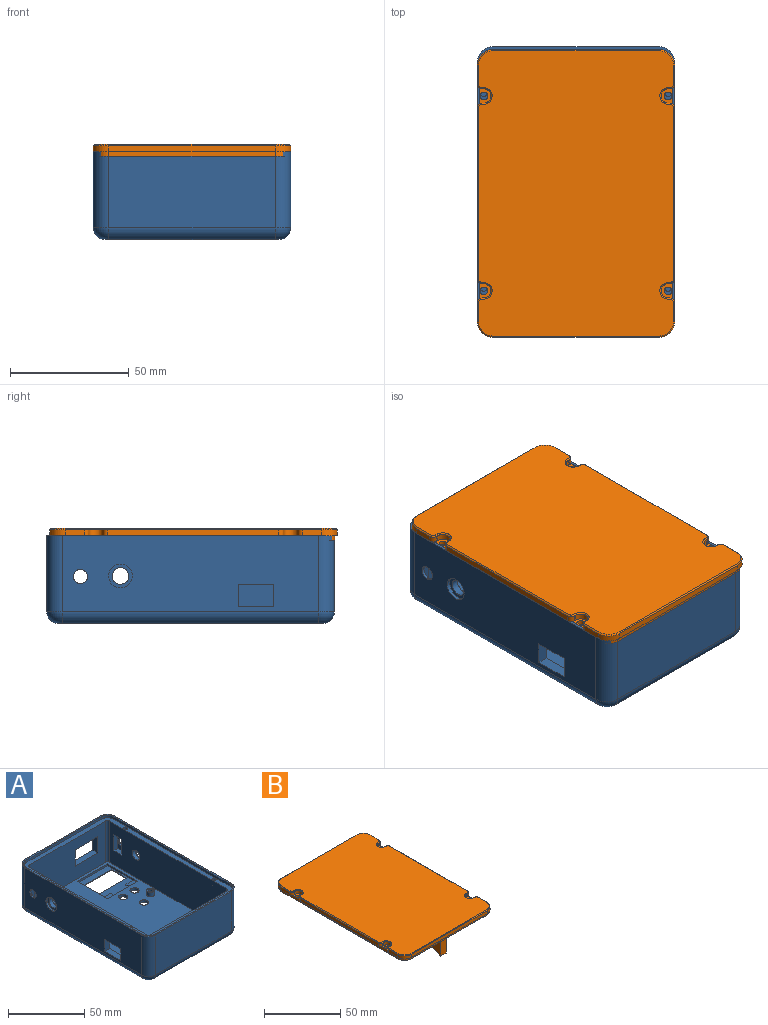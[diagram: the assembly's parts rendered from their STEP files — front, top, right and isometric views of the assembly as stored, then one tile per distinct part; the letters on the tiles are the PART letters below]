
ASSEMBLY  parts=2 mates=1
PART A: 103 faces, bbox 83x121x37 mm
  f0: plane 119x81mm, normal (0,0,1), area 1303.8mm2, adj f4,f12,f13,f14,f15,f16,f17,f18
  f1: cylinder r=3.5mm len=7mm, axis (1,0,0), area 66mm2, adj f12,f61
  f2: cylinder r=3mm len=6mm, axis (-1,0,0), area 18.8mm2, adj f23,f59
  f3: cylinder r=3.5mm len=7mm, axis (-1,0,0), area 66mm2, adj f4,f54
  f4: plane 108x33mm, normal (1,0,0), area 3292.4mm2, adj f0,f3,f6,f17,f18,f48,f49,f50
  f5: cylinder r=3mm len=6mm, axis (1,0,0), area 18.8mm2, adj f19,f52
  f6: plane 112x74mm, normal (0,0,1), area 7272mm2, adj f4,f12,f13,f14,f15,f16,f17,f18
  f7: plane 26x0.5mm, normal (0,1,0), area 13mm2, adj f8,f9,f11,f38
  f8: plane 14x0.5mm, normal (1,0,0), area 7mm2, adj f7,f10,f11,f38
  f9: plane 14x0.5mm, normal (-1,0,0), area 7mm2, adj f7,f10,f11,f38
  f10: plane 26x0.5mm, normal (0,-1,0), area 13mm2, adj f8,f9,f11,f38
  f11: plane 111x73mm, normal (0,0,-1), area 7567.4mm2, adj f7,f8,f9,f10,f42,f43,f44,f45
  f12: plane 108x33mm, normal (-1,0,0), area 3434.9mm2, adj f0,f1,f6,f15,f16,f55,f56,f57
  f13: plane 70x33mm, normal (0,-1,0), area 2037mm2, adj f0,f6,f15,f18,f27,f28,f29,f30
  f14: plane 70x33mm, normal (0,1,0), area 2310mm2, adj f0,f6,f16,f17
  f15: cylinder r=2mm len=33mm, axis (0,0,-1), area 103.7mm2, adj f0,f6,f12,f13
  f16: cylinder r=2mm len=33mm, axis (0,0,-1), area 103.7mm2, adj f0,f6,f12,f14
  f17: cylinder r=2mm len=33mm, axis (0,0,-1), area 103.7mm2, adj f0,f4,f6,f14
  f18: cylinder r=2mm len=33mm, axis (0,0,-1), area 103.7mm2, adj f0,f4,f6,f13
  f19: plane 108x32mm, normal (-1,0,0), area 3206.7mm2, adj f5,f20,f26,f53,f70,f71,f72,f73
  f20: cylinder r=6.5mm len=32mm, axis (0,0,-1), area 326.7mm2, adj f19,f21,f70,f89
  f21: plane 70x32mm, normal (0,-1,0), area 2240mm2, adj f20,f22,f70,f87
  f22: cylinder r=6.5mm len=32mm, axis (0,0,-1), area 326.7mm2, adj f21,f23,f70,f85
  f23: plane 108x32mm, normal (1,0,0), area 3349.2mm2, adj f2,f22,f24,f60,f70,f84
  f24: cylinder r=6.5mm len=32mm, axis (0,0,-1), area 326.7mm2, adj f23,f25,f70,f86
  f25: plane 70x32mm, normal (0,1,0), area 1967mm2, adj f24,f26,f27,f28,f29,f30,f70,f88
  f26: cylinder r=6.5mm len=32mm, axis (0,0,-1), area 326.7mm2, adj f19,f25,f70,f90
  f27: plane 21x4.5mm, normal (0,0,1), area 94.5mm2, adj f13,f25,f28,f29
  f28: plane 13x4.5mm, normal (-1,0,0), area 58.5mm2, adj f13,f25,f27,f30
  f29: plane 13x4.5mm, normal (1,0,0), area 58.5mm2, adj f13,f25,f27,f30
  f30: plane 21x4.5mm, normal (0,0,-1), area 94.5mm2, adj f13,f25,f28,f29
  f31: plane 28x1.5mm, normal (-1,0,0), area 40mm2, adj f6,f35,f37,f38,f39,f41
  f32: plane 28x1.5mm, normal (1,0,0), area 40mm2, adj f6,f33,f35,f38,f40,f41
  f33: plane 7x0.5mm, normal (0,1,0), area 3.5mm2, adj f32,f34,f38,f40
  f34: plane 4x0.5mm, normal (1,0,0), area 2mm2, adj f33,f35,f38,f40
  f35: plane 28x1.5mm, normal (0,1,0), area 35mm2, adj f6,f31,f32,f34,f36,f38,f39,f40
  f36: plane 4x0.5mm, normal (-1,0,0), area 2mm2, adj f35,f37,f38,f39
  f37: plane 7x0.5mm, normal (0,1,0), area 3.5mm2, adj f31,f36,f38,f39
  f38: plane 28x28mm, normal (0,0,1), area 364mm2, adj f7,f8,f9,f10,f31,f32,f33,f34
  f39: plane 7x4mm, normal (0,0,1), area 28mm2, adj f31,f35,f36,f37
  f40: plane 7x4mm, normal (0,0,1), area 28mm2, adj f32,f33,f34,f35
  f41: plane 28x1.5mm, normal (0,-1,0), area 42mm2, adj f6,f31,f32,f38
  f42: cylinder r=3mm len=6mm, axis (0,0,1), area 37.7mm2, adj f6,f11
  f43: cylinder r=3mm len=6mm, axis (0,0,1), area 37.7mm2, adj f6,f11
  f44: cylinder r=3mm len=6mm, axis (0,0,1), area 37.7mm2, adj f6,f11
  f45: cylinder r=3mm len=6mm, axis (0,0,1), area 37.7mm2, adj f6,f11
  f46: cylinder r=3mm len=6mm, axis (0,0,1), area 37.7mm2, adj f6,f11
  f47: cylinder r=3mm len=6mm, axis (0,0,1), area 37.7mm2, adj f6,f11
  f48: plane 12.5x3.5mm, normal (0,-1,0), area 43.8mm2, adj f4,f49,f51,f52
  f49: plane 7.25x3.5mm, normal (0,0,-1), area 25.4mm2, adj f4,f48,f50,f52
  f50: plane 12.5x3.5mm, normal (0,1,0), area 43.8mm2, adj f4,f49,f51,f52
  f51: plane 7.25x3.5mm, normal (0,0,1), area 25.4mm2, adj f4,f48,f50,f52
  f52: plane 12.5x7.25mm, normal (1,0,0), area 62.4mm2, adj f5,f48,f49,f50,f51
  f53: cylinder r=5mm len=10mm, axis (-1,0,0), area 47.1mm2, adj f19,f54
  f54: plane 10x10mm, normal (-1,0,0), area 40.1mm2, adj f3,f53
  f55: plane 12.5x3.5mm, normal (0,-1,0), area 43.8mm2, adj f12,f56,f58,f59
  f56: plane 7.25x3.5mm, normal (0,0,1), area 25.4mm2, adj f12,f55,f57,f59
  f57: plane 12.5x3.5mm, normal (0,1,0), area 43.8mm2, adj f12,f56,f58,f59
  f58: plane 7.25x3.5mm, normal (0,0,-1), area 25.4mm2, adj f12,f55,f57,f59
  f59: plane 12.5x7.25mm, normal (-1,0,0), area 62.4mm2, adj f2,f55,f56,f57,f58
  f60: cylinder r=5mm len=10mm, axis (1,0,0), area 47.1mm2, adj f23,f61
  f61: plane 10x10mm, normal (1,0,0), area 40.1mm2, adj f1,f60
  f62: cylinder r=5.5mm len=5.5mm, axis (0,0,-1), area 17.3mm2, adj f0,f63,f69,f70
  f63: plane 108x2mm, normal (1,0,0), area 216mm2, adj f0,f62,f64,f70
  f64: cylinder r=5.5mm len=5.5mm, axis (0,0,-1), area 17.3mm2, adj f0,f63,f65,f70
  f65: plane 70x2mm, normal (0,-1,0), area 140mm2, adj f0,f64,f66,f70
  f66: cylinder r=5.5mm len=5.5mm, axis (0,0,-1), area 17.3mm2, adj f0,f65,f67,f70
  f67: plane 108x2mm, normal (-1,0,0), area 216mm2, adj f0,f66,f68,f70
  f68: cylinder r=5.5mm len=5.5mm, axis (0,0,-1), area 17.3mm2, adj f0,f67,f69,f70
  f69: plane 70x2mm, normal (0,1,0), area 140mm2, adj f0,f62,f68,f70
  f70: plane 121x83mm, normal (0,0,1), area 393.7mm2, adj f19,f20,f21,f22,f23,f24,f25,f26
  f71: plane 9.5x4.5mm, normal (0,1,0), area 42.8mm2, adj f4,f19,f72,f73
  f72: plane 15x4.5mm, normal (0,0,1), area 67.5mm2, adj f4,f19,f71,f74
  f73: plane 15x4.5mm, normal (0,0,-1), area 67.5mm2, adj f4,f19,f71,f74
  f74: plane 9.5x4.5mm, normal (0,-1,0), area 42.8mm2, adj f4,f19,f72,f73
  f75: cylinder r=1.45mm len=4.5mm, axis (0,0,-1), area 41mm2, adj f77,f102
  f76: cylinder r=2.5mm len=5mm, axis (0,0,-1), area 55mm2, adj f6,f77
  f77: plane 5x5mm, normal (0,0,1), area 13mm2, adj f75,f76
  f78: cylinder r=1.45mm len=4.5mm, axis (0,0,-1), area 41mm2, adj f80,f101
  f79: cylinder r=2.5mm len=5mm, axis (0,0,-1), area 55mm2, adj f6,f80
  f80: plane 5x5mm, normal (0,0,1), area 13mm2, adj f78,f79
  f81: cylinder r=1.45mm len=4.5mm, axis (0,0,-1), area 41mm2, adj f83,f100
  f82: cylinder r=2.5mm len=5mm, axis (0,0,-1), area 55mm2, adj f6,f83
  f83: plane 5x5mm, normal (0,0,1), area 13mm2, adj f81,f82
  f84: cylinder r=5mm len=108mm, axis (0,1,0), area 848.2mm2, adj f11,f23,f85,f86
  f85: torus R=1.5mm, axis (0,0,1), area 57.8mm2, adj f11,f22,f84,f87
  f86: torus R=1.5mm, axis (0,0,1), area 57.8mm2, adj f11,f24,f84,f88
  f87: cylinder r=5mm len=70mm, axis (1,0,0), area 549.8mm2, adj f11,f21,f85,f89
  f88: cylinder r=5mm len=70mm, axis (-1,0,0), area 549.8mm2, adj f11,f25,f86,f90
  f89: torus R=1.5mm, axis (0,0,1), area 57.8mm2, adj f11,f20,f87,f91
  f90: torus R=1.5mm, axis (0,0,1), area 57.8mm2, adj f11,f26,f88,f91
  f91: cylinder r=5mm len=108mm, axis (0,-1,0), area 848.2mm2, adj f11,f19,f89,f90
  f92: cylinder r=1.4mm len=4mm, axis (0,0,1), area 35.2mm2, adj f0,f93
  f93: plane 2.8x2.8mm, normal (0,0,1), area 6.2mm2, adj f92
  f94: cylinder r=1.4mm len=4mm, axis (0,0,1), area 35.2mm2, adj f0,f95
  f95: plane 2.8x2.8mm, normal (0,0,1), area 6.2mm2, adj f94
  f96: cylinder r=1.4mm len=4mm, axis (0,0,1), area 35.2mm2, adj f0,f97
  f97: plane 2.8x2.8mm, normal (0,0,1), area 6.2mm2, adj f96
  f98: cylinder r=1.4mm len=4mm, axis (0,0,1), area 35.2mm2, adj f0,f99
  f99: plane 2.8x2.8mm, normal (0,0,1), area 6.2mm2, adj f98
  f100: plane 2.9x2.9mm, normal (0,0,1), area 6.6mm2, adj f81
  f101: plane 2.9x2.9mm, normal (0,0,1), area 6.6mm2, adj f78
  f102: plane 2.9x2.9mm, normal (0,0,1), area 6.6mm2, adj f75
PART B: 99 faces, bbox 83x121x21 mm
  f0: cylinder r=1.6mm len=3.2mm, axis (0,0,-1), area 15.5mm2, adj f21,f33,f98
  f1: cylinder r=1.6mm len=3.2mm, axis (0,0,-1), area 15.5mm2, adj f21,f42,f97
  f2: cylinder r=1.6mm len=3.2mm, axis (0,0,-1), area 15.5mm2, adj f21,f38,f96
  f3: cylinder r=1.6mm len=3.2mm, axis (0,0,-1), area 15.5mm2, adj f21,f37,f95
  f4: plane 72x2.5mm, normal (-1,0,0), area 180mm2, adj f11,f50,f52,f74
  f5: plane 8x2.5mm, normal (-1,0,0), area 20mm2, adj f8,f29,f53,f63
  f6: plane 8x2.5mm, normal (1,0,0), area 20mm2, adj f8,f27,f46,f71
  f7: plane 72x2.5mm, normal (1,0,0), area 180mm2, adj f9,f47,f48,f83
  f8: plane 83x16.23mm, normal (0,0,-1), area 107.3mm2, adj f5,f6,f13,f17,f18,f19,f20,f27
  f9: plane 75.46x1mm, normal (0,0,-1), area 74.5mm2, adj f7,f17,f47,f48
  f10: plane 83x16.23mm, normal (0,0,-1), area 107.3mm2, adj f13,f14,f15,f16,f17,f22,f23,f24
  f11: plane 75.46x1mm, normal (0,0,-1), area 74.5mm2, adj f4,f13,f50,f52
  f12: plane 120x82mm, normal (0,0,1), area 9666.7mm2, adj f63,f64,f65,f66,f67,f68,f69,f70
  f13: plane 108x2mm, normal (-1,0,0), area 216mm2, adj f8,f10,f11,f14,f20,f21,f33,f37
  f14: cylinder r=5.5mm len=5.5mm, axis (0,0,-1), area 17.3mm2, adj f10,f13,f15,f21
  f15: plane 70x2mm, normal (0,-1,0), area 140mm2, adj f10,f14,f16,f21
  f16: cylinder r=5.5mm len=5.5mm, axis (0,0,-1), area 17.3mm2, adj f10,f15,f17,f21
  f17: plane 108x2mm, normal (1,0,0), area 216mm2, adj f8,f9,f10,f16,f18,f21,f38,f42
  f18: cylinder r=5.5mm len=5.5mm, axis (0,0,-1), area 17.3mm2, adj f8,f17,f19,f21
  f19: plane 70x2mm, normal (0,1,0), area 140mm2, adj f8,f18,f20,f21
  f20: cylinder r=5.5mm len=5.5mm, axis (0,0,-1), area 17.3mm2, adj f8,f13,f19,f21
  f21: plane 119x81mm, normal (0,0,-1), area 9343.2mm2, adj f0,f1,f2,f3,f13,f14,f15,f16
  f22: plane 8x2.5mm, normal (-1,0,0), area 20mm2, adj f10,f23,f51,f86
  f23: cylinder r=6.5mm len=6.5mm, axis (0,0,-1), area 25.5mm2, adj f10,f22,f24,f88
  f24: plane 70x2.5mm, normal (0,-1,0), area 175mm2, adj f10,f23,f25,f90
  f25: cylinder r=6.5mm len=6.5mm, axis (0,0,-1), area 25.5mm2, adj f10,f24,f26,f92
  f26: plane 8x2.5mm, normal (1,0,0), area 20mm2, adj f10,f25,f49,f94
  f27: cylinder r=6.5mm len=6.5mm, axis (0,0,-1), area 25.5mm2, adj f6,f8,f28,f69
  f28: plane 70x2.5mm, normal (0,1,0), area 175mm2, adj f8,f27,f29,f67
  f29: cylinder r=6.5mm len=6.5mm, axis (0,0,-1), area 25.5mm2, adj f5,f8,f28,f65
  f30: plane 2.5x0.7mm, normal (0,1,0), area 1.7mm2, adj f31,f33,f52,f70
  f31: cylinder r=3mm len=6mm, axis (0,0,1), area 23.6mm2, adj f30,f32,f33,f68
  f32: plane 2.5x0.7mm, normal (0,-1,0), area 1.7mm2, adj f31,f33,f53,f66
  f33: plane 6.54x4.7mm, normal (0,0,1), area 17mm2, adj f0,f13,f30,f31,f32,f52,f53,f98
  f34: cylinder r=3mm len=6mm, axis (0,0,1), area 23.6mm2, adj f35,f36,f37,f80
  f35: plane 2.5x0.7mm, normal (0,-1,0), area 1.7mm2, adj f34,f37,f50,f78
  f36: plane 2.5x0.7mm, normal (0,1,0), area 1.7mm2, adj f34,f37,f51,f82
  f37: plane 6.54x4.7mm, normal (0,0,1), area 17mm2, adj f3,f13,f34,f35,f36,f50,f51,f95
  f38: plane 6.54x4.7mm, normal (0,0,1), area 17mm2, adj f2,f17,f39,f40,f41,f48,f49,f96
  f39: plane 2.5x0.7mm, normal (0,-1,0), area 1.7mm2, adj f38,f40,f48,f87
  f40: cylinder r=3mm len=6mm, axis (0,0,1), area 23.6mm2, adj f38,f39,f41,f89
  f41: plane 2.5x0.7mm, normal (0,1,0), area 1.7mm2, adj f38,f40,f49,f91
  f42: plane 6.54x4.7mm, normal (0,0,1), area 17mm2, adj f1,f17,f43,f44,f45,f46,f47,f97
  f43: plane 2.5x0.7mm, normal (0,-1,0), area 1.7mm2, adj f42,f44,f46,f75
  f44: cylinder r=3mm len=6mm, axis (0,0,1), area 23.6mm2, adj f42,f43,f45,f77
  f45: plane 2.5x0.7mm, normal (0,1,0), area 1.7mm2, adj f42,f44,f47,f79
  f46: cylinder r=2mm len=2.5mm, axis (0,0,-1), area 7.9mm2, adj f6,f8,f42,f43,f73
  f47: cylinder r=2mm len=2.5mm, axis (0,0,-1), area 7.9mm2, adj f7,f9,f42,f45,f81
  f48: cylinder r=2mm len=2.5mm, axis (0,0,-1), area 7.9mm2, adj f7,f9,f38,f39,f85
  f49: cylinder r=2mm len=2.5mm, axis (0,0,-1), area 7.9mm2, adj f10,f26,f38,f41,f93
  f50: cylinder r=2mm len=2.5mm, axis (0,0,-1), area 7.9mm2, adj f4,f11,f35,f37,f76
  f51: cylinder r=2mm len=2.5mm, axis (0,0,-1), area 7.9mm2, adj f10,f22,f36,f37,f84
  f52: cylinder r=2mm len=2.5mm, axis (0,0,1), area 7.9mm2, adj f4,f11,f30,f33,f72
  f53: cylinder r=2mm len=2.5mm, axis (0,0,1), area 7.9mm2, adj f5,f8,f32,f33,f64
  f54: plane 16x15mm, normal (0,-1,0), area 90.7mm2, adj f21,f55,f57,f60,f61,f62
  f55: plane 16x11mm, normal (-1,0,0), area 148mm2, adj f54,f56,f58,f59,f60,f61
  f56: plane 16x15mm, normal (0,1,0), area 90.7mm2, adj f21,f55,f57,f58,f61,f62
  f57: plane 16x11mm, normal (1,0,0), area 148mm2, adj f54,f56,f58,f59,f60,f62
  f58: plane 5x1.25mm, normal (0,0,-1), area 6.2mm2, adj f55,f56,f57,f59
  f59: cylinder r=9.1mm len=13.51mm, axis (-1,0,0), area 76.1mm2, adj f55,f57,f58,f60
  f60: plane 5x1.25mm, normal (0,0,-1), area 6.2mm2, adj f54,f55,f57,f59
  f61: cylinder r=5mm len=16mm, axis (0,-1,0), area 125.7mm2, adj f21,f54,f55,f56
  f62: cylinder r=5mm len=16mm, axis (0,1,0), area 125.7mm2, adj f21,f54,f56,f57
  f63: plane 8x0.5mm, normal (-0.71,0,0.71), area 5.7mm2, adj f5,f12,f64,f65
  f64: cone r=1.5mm half-angle=45deg, axis (0,0,-1), area 1.9mm2, adj f12,f53,f63,f66
  f65: cone r=6mm half-angle=45deg, axis (0,0,-1), area 6.9mm2, adj f12,f29,f63,f67
  f66: plane 0.7x0.5mm, normal (0,-0.71,0.71), area 0.5mm2, adj f12,f32,f64,f68
  f67: plane 70x0.5mm, normal (0,0.71,0.71), area 49.5mm2, adj f12,f28,f65,f69
  f68: cone r=3mm half-angle=45deg, axis (0,0,1), area 7.2mm2, adj f12,f31,f66,f70
  f69: cone r=6mm half-angle=45deg, axis (0,0,-1), area 6.9mm2, adj f12,f27,f67,f71
  f70: plane 0.7x0.5mm, normal (0,0.71,0.71), area 0.5mm2, adj f12,f30,f68,f72
  f71: plane 8x0.5mm, normal (0.71,0,0.71), area 5.7mm2, adj f6,f12,f69,f73
  f72: cone r=1.5mm half-angle=45deg, axis (0,0,-1), area 1.9mm2, adj f12,f52,f70,f74
  f73: cone r=1.5mm half-angle=45deg, axis (0,0,-1), area 1.9mm2, adj f12,f46,f71,f75
  f74: plane 72x0.5mm, normal (-0.71,0,0.71), area 50.9mm2, adj f4,f12,f72,f76
  f75: plane 0.7x0.5mm, normal (0,-0.71,0.71), area 0.5mm2, adj f12,f43,f73,f77
  f76: cone r=1.5mm half-angle=45deg, axis (0,0,-1), area 1.9mm2, adj f12,f50,f74,f78
  f77: cone r=3mm half-angle=45deg, axis (0,0,1), area 7.2mm2, adj f12,f44,f75,f79
  f78: plane 0.7x0.5mm, normal (0,-0.71,0.71), area 0.5mm2, adj f12,f35,f76,f80
  f79: plane 0.7x0.5mm, normal (0,0.71,0.71), area 0.5mm2, adj f12,f45,f77,f81
  f80: cone r=3mm half-angle=45deg, axis (0,0,1), area 7.2mm2, adj f12,f34,f78,f82
  f81: cone r=1.5mm half-angle=45deg, axis (0,0,-1), area 1.9mm2, adj f12,f47,f79,f83
  f82: plane 0.7x0.5mm, normal (0,0.71,0.71), area 0.5mm2, adj f12,f36,f80,f84
  f83: plane 72x0.5mm, normal (0.71,0,0.71), area 50.9mm2, adj f7,f12,f81,f85
  f84: cone r=1.5mm half-angle=45deg, axis (0,0,-1), area 1.9mm2, adj f12,f51,f82,f86
  f85: cone r=1.5mm half-angle=45deg, axis (0,0,-1), area 1.9mm2, adj f12,f48,f83,f87
  f86: plane 8x0.5mm, normal (-0.71,0,0.71), area 5.7mm2, adj f12,f22,f84,f88
  f87: plane 0.7x0.5mm, normal (0,-0.71,0.71), area 0.5mm2, adj f12,f39,f85,f89
  f88: cone r=6mm half-angle=45deg, axis (0,0,-1), area 6.9mm2, adj f12,f23,f86,f90
  f89: cone r=3mm half-angle=45deg, axis (0,0,1), area 7.2mm2, adj f12,f40,f87,f91
  f90: plane 70x0.5mm, normal (0,-0.71,0.71), area 49.5mm2, adj f12,f24,f88,f92
  f91: plane 0.7x0.5mm, normal (0,0.71,0.71), area 0.5mm2, adj f12,f41,f89,f93
  f92: cone r=6mm half-angle=45deg, axis (0,0,-1), area 6.9mm2, adj f12,f25,f90,f94
  f93: cone r=1.5mm half-angle=45deg, axis (0,0,-1), area 1.9mm2, adj f12,f49,f91,f94
  f94: plane 8x0.5mm, normal (0.71,0,0.71), area 5.7mm2, adj f12,f26,f92,f93
  f95: plane 2.12x2mm, normal (1,0,0), area 4.2mm2, adj f3,f21,f37
  f96: plane 2.12x2mm, normal (-1,0,0), area 4.2mm2, adj f2,f21,f38
  f97: plane 2.12x2mm, normal (-1,0,0), area 4.2mm2, adj f1,f21,f42
  f98: plane 2.12x2mm, normal (1,0,0), area 4.2mm2, adj f0,f21,f33
PLACE A t=(2.42,-29.87,44.55)mm
PLACE B t=(2.42,-31.08,42.55)mm
MATE slider A.f0 <-> B.f21  axis (0,0,1) through (2.42,26.13,79.55)mm
